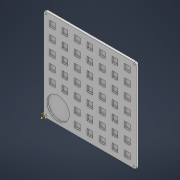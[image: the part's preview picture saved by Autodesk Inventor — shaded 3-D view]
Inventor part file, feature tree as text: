
AUTODESK INVENTOR PART (.ipt)
format: ipt  version: 2022 (Build 260153000, 153)  size: 300,544 bytes
history: native  units: mm
features: sketch x8, extrude x6, pattern_linear x2, fillet x2
ambient origin geometry x8: Origin, YZ Plane, XZ Plane, XY Plane, X Axis, Y Axis, Z Axis, Center Point
bodies: Solid1 (feature_tree)
feature tree (18):
  extrude  "Extrusion1"  Depth=220.0mm
  extrude  "Extrusion2"  Depth=5.0mm
  pattern_linear  "Rectangular Pattern1"  Count1=20  [1 undecoded]
  extrude  "Extrusion4"  Depth=28.5mm
  pattern_linear  "Rectangular Pattern2"  Count1=7 Spacing1=28.5mm
  extrude  "Extrusion5"  Depth=28.5mm
  sketch  "Sketch6"  dims[d14=50.0mm d16=28.5mm d17=200.0mm]
  extrude  "Extrusion3"  Depth=55.0mm
  fillet  "Fillet1"  Radius=55.0mm
  extrude  "Extrusion12"  Depth=3.0mm TaperAngle=0.0deg
  fillet  "Fillet4"  Radius=200.0mm
  sketch  "Sketch16"  dims[d21=51.0mm d22=3.0mm d23=0.0mm d24=200.0mm d25=200.0mm d26=28.5mm d27=20.5mm d28=3.0mm d29=0.0mm d30=20.0mm d32=28.5mm d33=50.0mm d35=28.5mm d36=5.0mm d37=5.0mm d38=3.2mm d39=10.0mm d40=0.0mm d41=13.0mm d42=13.0mm d43=13.0mm d44=13.0mm d45=2.0mm d60=2.75mm d79=220.0mm d80=220.0mm d81=210.0mm d82=210.0mm d83=5.0mm d84=0.0mm d85=200.0mm d86=200.0mm d87=3.5mm d88=20.0mm d90=200.0mm d91=20.0mm d93=200.0mm d96=4.0mm]
  sketch  "Sketch1"  dims[d0=220.0mm d1=220.0mm]
  sketch  "Sketch2"  dims[d2=5.0mm d3=0.0mm d4=200.0mm d5=200.0mm]
  sketch  "Sketch3"  dims[d6=28.5mm d7=28.5mm]
  sketch  "Sketch4"  dims[d8=20.5mm]
  sketch  "Sketch5"  dims[d9=3.0mm d10=0.0mm d11=70.0mm d13=28.5mm]
  sketch  "Sketch15"  dims[d18=200.0mm d19=55.0mm d20=55.0mm]
note: 1 required parameter value undecoded (feature->parameter linkage not recoverable at this tier; creation-order binding heuristic only, values carry confidence <= 0.55)
